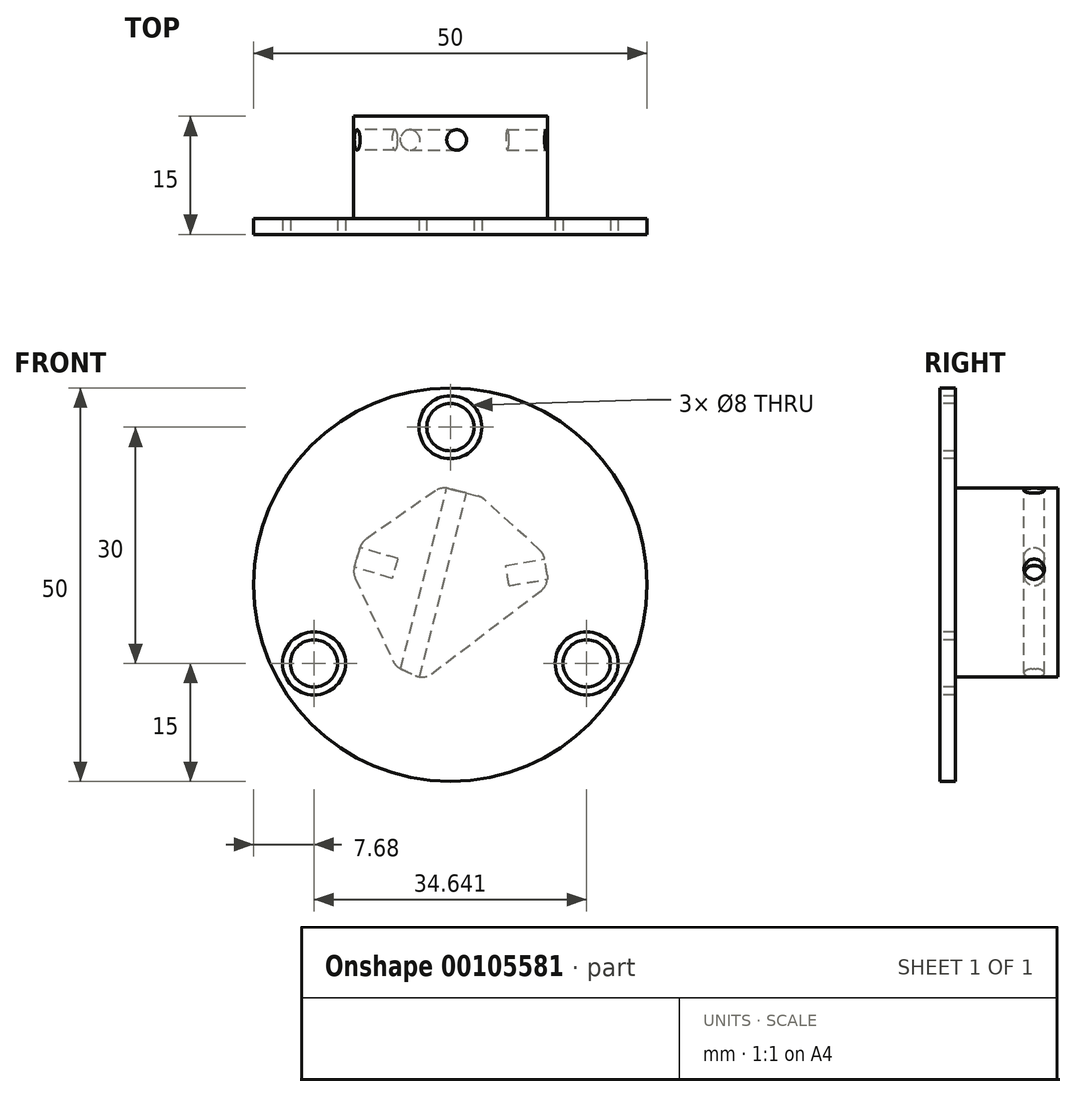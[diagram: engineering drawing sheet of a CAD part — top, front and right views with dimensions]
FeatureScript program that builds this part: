
annotation { "Feature Type Name" : "Feature", "Feature Type Description" : "" }
export const myFeature = defineFeature(function(context is Context, id is Id, definition is map)
    precondition{}
    {
        {
            var Q0;
            Q0=qCreatedBy(makeId("Front.planeOp"),FACE);
            var sketch = newSketch(context, id + "F0", { "sketchPlane" : qUnion([Q0])});
            skCircle(sketch, "E0", {"center": v(0, 0) * mm, "radius": 12.5 * mm, "construction": true});
            skLineSegment(sketch, "E1", {"start": v(12.5, 0) * mm, "end": v(11.86, 3.95) * mm});
            skLineSegment(sketch, "E2", {"start": v(11.86, 3.95) * mm, "end": v(2.85, 12.17) * mm});
            skLineSegment(sketch, "E3", {"start": v(2.85, 12.17) * mm, "end": v(-1.14, 12.45) * mm, "construction": true});
            skLineSegment(sketch, "E4", {"start": v(-1.14, 12.45) * mm, "end": v(-11.28, 5.4) * mm});
            skLineSegment(sketch, "E5", {"start": v(-11.28, 5.4) * mm, "end": v(-12.4, 1.55) * mm});
            skLineSegment(sketch, "E6", {"start": v(-12.4, 1.55) * mm, "end": v(-6.98, -10.37) * mm});
            skLineSegment(sketch, "E7", {"start": v(-6.98, -10.37) * mm, "end": v(-3.34, -12.04) * mm});
            skLineSegment(sketch, "E8", {"start": v(-3.34, -12.04) * mm, "end": v(12.5, 0) * mm});
            skLineSegment(sketch, "E9", {"start": v(0.85, 12.3) * mm, "end": v(-5.16, -11.2) * mm, "construction": true});
            skLineSegment(sketch, "E10", {"start": v(-1.14, 12.45) * mm, "end": v(3.98, 11.14) * mm});
            skSolve(sketch);
        }
        {
            var Q0;
            Q0=makeQuery(id+"F0.imprint","IMPRINT",FACE,{"disambiguationData":[TD([[makeQuery(id+"F0.imprint","IMPRINT",EDGE,{"derivedFrom":sQuery(id+"F0.wireOp",EDGE,"E1")}),1.0]])]});
            extrude(context, id + "F1", {"entities" : qUnion([Q0]), "depth" : 13 * mm});
        }
        {
            var Q0;
            Q0=makeQuery(id+"F1.opExtrude","SWEPT_FACE",FACE,{"disambiguationData":[OSD([sQuery(id+"F0.wireOp",EDGE,"E1")])]});
            var sketch = newSketch(context, id + "F2", { "sketchPlane" : qUnion([Q0])});
            skCircle(sketch, "E11", {"center": v(-3, 0) * mm, "radius": 1.3 * mm});
            skSolve(sketch);
        }
        {
            var Q0;
            Q0 = qSketchRegion(id + "F2", true);
            extrude(context, id + "F3", {"entities" : qUnion([Q0]), "operationType" : NewBodyOperationType.REMOVE, "oppositeDirection" : true, "depth" : 5 * mm});
        }
        {
            var Q0;
            Q0=makeQuery(id+"F1.opExtrude","SWEPT_FACE",FACE,{"disambiguationData":[OSD([sQuery(id+"F0.wireOp",EDGE,"E10")])]});
            var sketch = newSketch(context, id + "F4", { "sketchPlane" : qUnion([Q0])});
            skCircle(sketch, "E12", {"center": v(-2.2, -3) * mm, "radius": 1.3 * mm});
            skSolve(sketch);
        }
        {
            var Q0;
            Q0 = qSketchRegion(id + "F4", true);
            extrude(context, id + "F5", {"entities" : qUnion([Q0]), "operationType" : NewBodyOperationType.REMOVE, "oppositeDirection" : true, "depth" : 25 * mm});
        }
        {
            var Q0;
            Q0=makeQuery(id+"F1.opExtrude","SWEPT_FACE",FACE,{"disambiguationData":[OSD([sQuery(id+"F0.wireOp",EDGE,"E5")])]});
            var sketch = newSketch(context, id + "F6", { "sketchPlane" : qUnion([Q0])});
            skCircle(sketch, "E13", {"center": v(3, 0) * mm, "radius": 1.3 * mm});
            skSolve(sketch);
        }
        {
            var Q0;
            Q0 = qSketchRegion(id + "F6", true);
            extrude(context, id + "F7", {"entities" : qUnion([Q0]), "operationType" : NewBodyOperationType.REMOVE, "oppositeDirection" : true, "depth" : 5 * mm});
        }
        {
            var Q0;
            Q0=makeQuery(id+"F1.opExtrude","CAP_FACE",FACE,{"disambiguationData":[OSD([sQuery(id+"F0.wireOp",EDGE,"E1"),sQuery(id+"F0.wireOp",EDGE,"E2"),sQuery(id+"F0.wireOp",EDGE,"E3"),sQuery(id+"F0.wireOp",EDGE,"E4"),sQuery(id+"F0.wireOp",EDGE,"E5"),sQuery(id+"F0.wireOp",EDGE,"E6"),sQuery(id+"F0.wireOp",EDGE,"E7"),sQuery(id+"F0.wireOp",EDGE,"E8")])],"isStart":false});
            var sketch = newSketch(context, id + "F8", { "sketchPlane" : qUnion([Q0])});
            skCircle(sketch, "E14", {"center": v(0, 0) * mm, "radius": 25 * mm});
            skSolve(sketch);
        }
        {
            var Q0;
            Q0 = qSketchRegion(id + "F8", true);
            extrude(context, id + "F9", {"entities" : qUnion([Q0]), "operationType" : NewBodyOperationType.ADD, "depth" : 2 * mm});
        }
        {
            var Q0;
            Q0=makeQuery(id+"F9.opExtrude","CAP_FACE",FACE,{"disambiguationData":[OSD([sQuery(id+"F8.wireOp",EDGE,"E14")])],"isStart":false});
            var sketch = newSketch(context, id + "F10", { "sketchPlane" : qUnion([Q0])});
            skCircle(sketch, "E15", {"center": v(0, 0) * mm, "radius": 20 * mm, "construction": true});
            skCircle(sketch, "E16", {"center": v(0, 20) * mm, "radius": 4 * mm});
            skCircle(sketch, "E17", {"center": v(17.32, -10) * mm, "radius": 4 * mm});
            skCircle(sketch, "E18", {"center": v(-17.32, -10) * mm, "radius": 4 * mm});
            skLineSegment(sketch, "E19", {"start": v(0, 0) * mm, "end": v(0, 20) * mm, "construction": true});
            skLineSegment(sketch, "E20", {"start": v(0, 0) * mm, "end": v(17.32, -10) * mm, "construction": true});
            skLineSegment(sketch, "E21", {"start": v(-17.32, -10) * mm, "end": v(0, 0) * mm, "construction": true});
            skCircle(sketch, "E22", {"center": v(-17.32, -10) * mm, "radius": 3 * mm});
            skCircle(sketch, "E23", {"center": v(17.32, -10) * mm, "radius": 3 * mm});
            skCircle(sketch, "E24", {"center": v(0, 20) * mm, "radius": 3 * mm});
            skSolve(sketch);
        }
        {
            var Q0;
            Q0 = qSketchRegion(id + "F10", true);
            extrude(context, id + "F11", {"entities" : qUnion([Q0]), "operationType" : NewBodyOperationType.REMOVE, "oppositeDirection" : true, "depth" : 80 * mm});
        }
        {
            var Q0;
            Q0=makeQuery(id+"F1.opExtrude","SWEPT_EDGE",EDGE,{"disambiguationData":[OSD([sQuery(id+"F0.wireOp",EDGE,"E7"),sQuery(id+"F0.wireOp",EDGE,"E8")])]});
            var Q1;
            Q1=makeQuery(id+"F1.opExtrude","SWEPT_EDGE",EDGE,{"disambiguationData":[OSD([sQuery(id+"F0.wireOp",EDGE,"E6"),sQuery(id+"F0.wireOp",EDGE,"E7")])]});
            var Q2;
            Q2=makeQuery(id+"F1.opExtrude","SWEPT_EDGE",EDGE,{"disambiguationData":[OSD([sQuery(id+"F0.wireOp",EDGE,"E5"),sQuery(id+"F0.wireOp",EDGE,"E6")])]});
            var Q3;
            Q3=makeQuery(id+"F1.opExtrude","SWEPT_EDGE",EDGE,{"disambiguationData":[OSD([sQuery(id+"F0.wireOp",EDGE,"E4"),sQuery(id+"F0.wireOp",EDGE,"E5")])]});
            var Q4;
            Q4=makeQuery(id+"F1.opExtrude","SWEPT_EDGE",EDGE,{"disambiguationData":[OSD([sQuery(id+"F0.wireOp",EDGE,"E3"),sQuery(id+"F0.wireOp",EDGE,"E4")])]});
            var Q5;
            Q5=makeQuery(id+"F1.opExtrude","SWEPT_EDGE",EDGE,{"disambiguationData":[OSD([sQuery(id+"F0.wireOp",EDGE,"E2"),sQuery(id+"F0.wireOp",EDGE,"E3")])]});
            var Q6;
            Q6=makeQuery(id+"F1.opExtrude","SWEPT_EDGE",EDGE,{"disambiguationData":[OSD([sQuery(id+"F0.wireOp",EDGE,"E1"),sQuery(id+"F0.wireOp",EDGE,"E2")])]});
            var Q7;
            Q7=makeQuery(id+"F1.opExtrude","SWEPT_EDGE",EDGE,{"disambiguationData":[OSD([sQuery(id+"F0.wireOp",EDGE,"E1"),sQuery(id+"F0.wireOp",EDGE,"E8")])]});
            fillet(context, id + "F12", {"entities" : qUnion([Q0, Q1, Q2, Q3, Q4, Q5, Q6, Q7]), "radius" : 2 * mm, "tangentPropagation" : true, "allowEdgeOverflow" : false});
        }
    });
